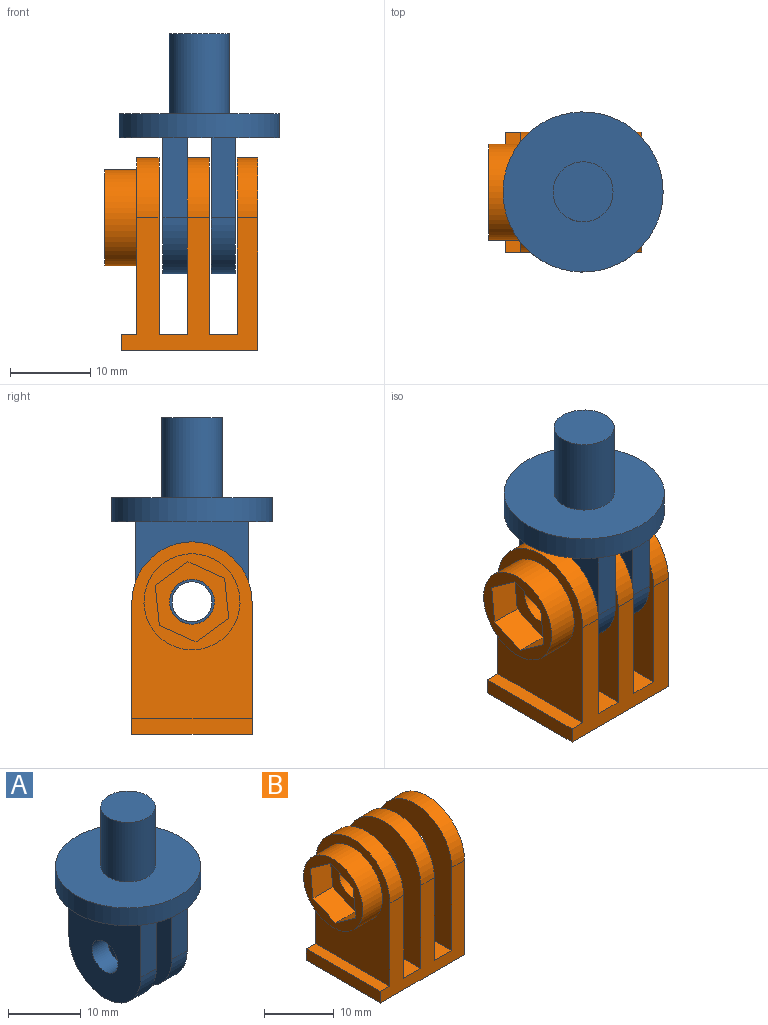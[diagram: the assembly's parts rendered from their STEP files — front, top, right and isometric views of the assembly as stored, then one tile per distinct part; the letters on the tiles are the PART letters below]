
ASSEMBLY  parts=2 mates=1
PART A: 17 faces, bbox 20x20x30 mm
  f0: plane 20x20mm, normal (0,0,-1), area 230.2mm2, adj f1,f5,f6,f7,f8,f9,f10,f11
  f1: cylinder r=10mm len=20mm, axis (0,0,1), area 188.5mm2, adj f0,f2
  f2: plane 20x20mm, normal (0,0,1), area 270mm2, adj f1,f3
  f3: cylinder r=3.75mm len=10mm, axis (0,0,1), area 235.6mm2, adj f2,f4
  f4: plane 7.5x7.5mm, normal (0,0,1), area 44.2mm2, adj f3
  f5: plane 17x14mm, normal (1,0,0), area 197.3mm2, adj f0,f6,f8,f14,f16
  f6: plane 10x3mm, normal (0,-1,0), area 30mm2, adj f0,f5,f7,f16
  f7: plane 17x14mm, normal (-1,0,0), area 197.3mm2, adj f0,f6,f8,f14,f16
  f8: plane 10x3mm, normal (0,1,0), area 30mm2, adj f0,f5,f7,f16
  f9: plane 17x14mm, normal (1,0,0), area 197.3mm2, adj f0,f10,f12,f13,f15
  f10: plane 10x3mm, normal (0,-1,0), area 30mm2, adj f0,f9,f11,f15
  f11: plane 17x14mm, normal (-1,0,0), area 197.3mm2, adj f0,f10,f12,f13,f15
  f12: plane 10x3mm, normal (0,1,0), area 30mm2, adj f0,f9,f11,f15
  f13: cylinder r=2.5mm len=5mm, axis (1,0,0), area 47.1mm2, adj f9,f11
  f14: cylinder r=2.5mm len=5mm, axis (1,0,0), area 47.1mm2, adj f5,f7
  f15: cylinder r=7mm len=14mm, axis (1,0,0), area 66mm2, adj f9,f10,f11,f12
  f16: cylinder r=7mm len=14mm, axis (1,0,0), area 66mm2, adj f5,f6,f7,f8
PART B: 28 faces, bbox 19.1x15x24 mm
  f0: plane 22.04x15mm, normal (-1,0,0), area 193.3mm2, adj f1,f9,f11,f14,f21
  f1: plane 17x16.54mm, normal (0,-1,0), area 151.9mm2, adj f0,f2,f3,f4,f5,f6,f7,f8
  f2: plane 24.04x15mm, normal (1,0,0), area 311.8mm2, adj f1,f9,f12,f15,f27
  f3: plane 22.04x15mm, normal (-1,0,0), area 281.8mm2, adj f1,f7,f9,f15,f27
  f4: plane 22.04x15mm, normal (1,0,0), area 281.8mm2, adj f1,f8,f9,f14,f25
  f5: plane 22.04x15mm, normal (1,0,0), area 281.8mm2, adj f1,f7,f9,f13,f26
  f6: plane 22.04x15mm, normal (-1,0,0), area 281.8mm2, adj f1,f8,f9,f13,f26
  f7: plane 15x3.5mm, normal (0,0,1), area 52.5mm2, adj f1,f3,f5,f9
  f8: plane 15x3.5mm, normal (0,0,1), area 52.5mm2, adj f1,f4,f6,f9
  f9: plane 17x16.54mm, normal (0,1,0), area 151.9mm2, adj f0,f2,f3,f4,f5,f6,f7,f8
  f10: plane 15x2mm, normal (-1,0,0), area 30mm2, adj f1,f9,f11,f12
  f11: plane 15x1.89mm, normal (0,0,1), area 28.4mm2, adj f0,f1,f9,f10
  f12: plane 17x15mm, normal (0,0,-1), area 255mm2, adj f1,f2,f9,f10
  f13: cylinder r=7.5mm len=15mm, axis (-1,0,0), area 64.8mm2, adj f1,f5,f6,f9
  f14: cylinder r=7.5mm len=15mm, axis (-1,0,0), area 65mm2, adj f0,f1,f4,f9
  f15: cylinder r=7.5mm len=15mm, axis (-1,0,0), area 61.2mm2, adj f1,f2,f3,f9
  f16: plane 4.58x4mm, normal (0,0.41,-0.91), area 20.1mm2, adj f17,f22,f23,f24
  f17: plane 5x4mm, normal (0,1,-0.1), area 20.1mm2, adj f16,f18,f23,f24
  f18: plane 4.08x4mm, normal (0,0.58,0.81), area 20.1mm2, adj f17,f19,f23,f24
  f19: plane 4.58x4mm, normal (0,-0.41,0.91), area 20.1mm2, adj f18,f20,f23,f24
  f20: plane 5x4mm, normal (0,-1,0.1), area 20.1mm2, adj f19,f22,f23,f24
  f21: cylinder r=6mm len=12mm, axis (-1,0,0), area 150.8mm2, adj f0,f23
  f22: plane 4.08x4mm, normal (0,-0.58,-0.81), area 20.1mm2, adj f16,f20,f23,f24
  f23: plane 12x12mm, normal (-1,0,0), area 47.4mm2, adj f16,f17,f18,f19,f20,f21,f22
  f24: plane 10.01x9.17mm, normal (-1,0,0), area 41.1mm2, adj f16,f17,f18,f19,f20,f22,f25
  f25: cylinder r=2.8mm len=5.6mm, axis (1,0,0), area 48.5mm2, adj f4,f24
  f26: cylinder r=2.8mm len=5.6mm, axis (1,0,0), area 48.4mm2, adj f5,f6
  f27: cylinder r=2.8mm len=5.6mm, axis (1,0,0), area 45.7mm2, adj f2,f3
PLACE A t=(-5.44,-4.49,14.67)mm
PLACE B t=(-6.32,-4.22,-11.88)mm
MATE revolute A.f15 <-> B.f25  axis (1,0,0) through (-6.94,-4.49,4.67)mm
